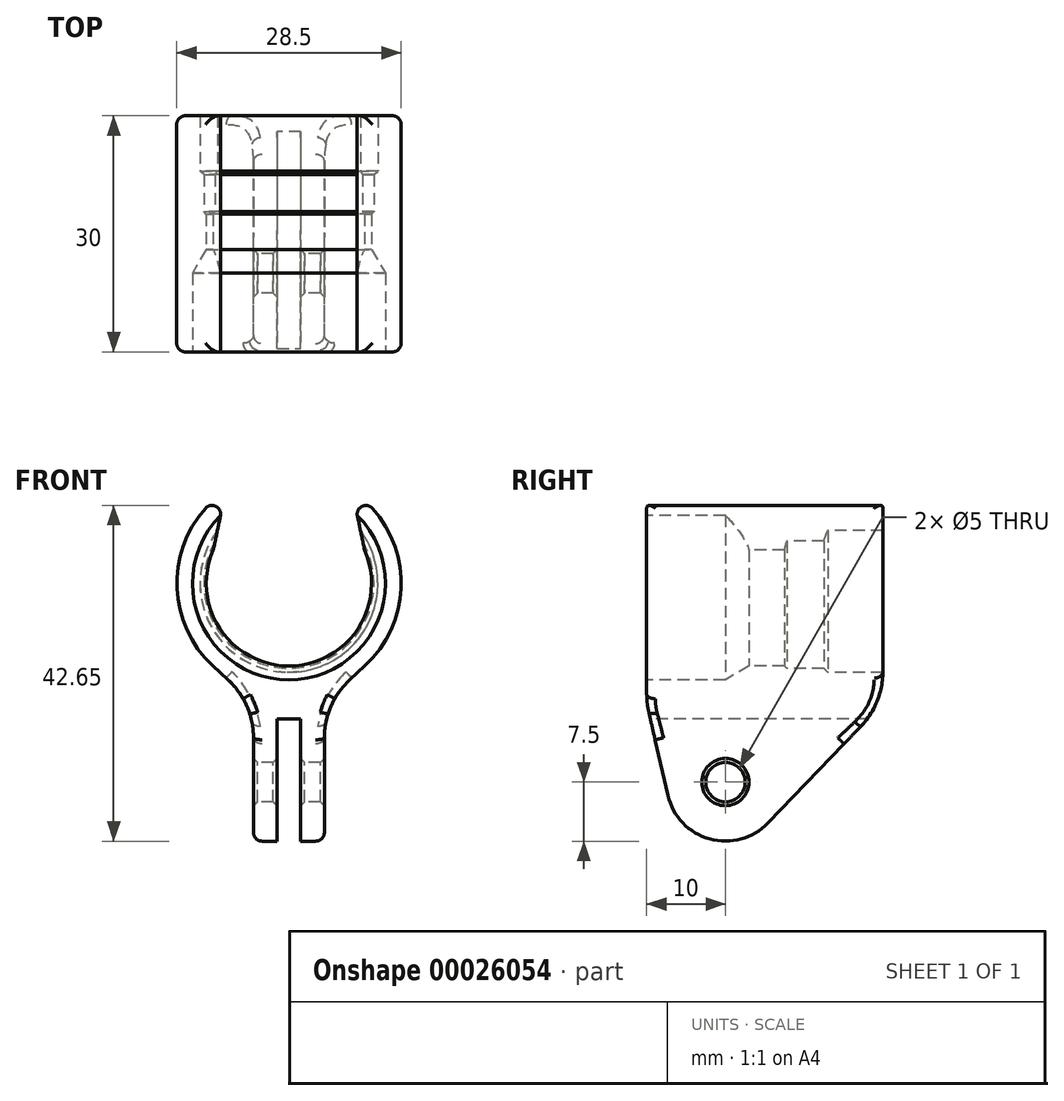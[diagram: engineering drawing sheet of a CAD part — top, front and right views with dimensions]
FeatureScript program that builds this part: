
annotation { "Feature Type Name" : "Feature", "Feature Type Description" : "" }
export const myFeature = defineFeature(function(context is Context, id is Id, definition is map)
    precondition{}
    {
        {
            var Q0;
            Q0=qCreatedBy(makeId("Right.planeOp"),FACE);
            var sketch = newSketch(context, id + "F0", { "sketchPlane" : qUnion([Q0])});
            skLineSegment(sketch, "E0", {"start": v(-10, 12.25) * mm, "end": v(-10, 14.25) * mm});
            skLineSegment(sketch, "E1", {"start": v(-10, 14.25) * mm, "end": v(20, 14.25) * mm});
            skLineSegment(sketch, "E2", {"start": v(20, 14.25) * mm, "end": v(20, 11.3) * mm});
            skLineSegment(sketch, "E3", {"start": v(20, 11.3) * mm, "end": v(13, 11.3) * mm});
            skLineSegment(sketch, "E4", {"start": v(13, 11.3) * mm, "end": v(13, 10.8) * mm});
            skLineSegment(sketch, "E5", {"start": v(13, 10.8) * mm, "end": v(8, 10.8) * mm});
            skLineSegment(sketch, "E6", {"start": v(8, 10.8) * mm, "end": v(8, 10.5) * mm});
            skLineSegment(sketch, "E7", {"start": v(8, 10.5) * mm, "end": v(3, 10.5) * mm});
            skLineSegment(sketch, "E8", {"start": v(0, 12.25) * mm, "end": v(-10, 12.25) * mm});
            skLineSegment(sketch, "E9", {"start": v(3, 10.5) * mm, "end": v(0, 12.25) * mm});
            skLineSegment(sketch, "E10", {"start": v(-10, 0) * mm, "end": v(20, 0) * mm, "construction": true});
            skSolve(sketch);
        }
        {
            var Q0;
            Q0 = qSketchRegion(id + "F0", true);
            var Q1;
            Q1=sQuery(id+"F0.wireOp",EDGE,"E10");
            var Q2;
            Q2=sQuery(id+"F0.wireOp",EDGE,"E10");
            revolve(context, id + "F1", {"entities" : qUnion([Q0]), "surfaceEntities" : qUnion([Q1]), "axis" : qUnion([Q2]), "revolveType" : RevolveType.FULL});
        }
        {
            var Q0;
            Q0=qCreatedBy(makeId("Front.planeOp"),FACE);
            var sketch = newSketch(context, id + "F2", { "sketchPlane" : qUnion([Q0])});
            skLineSegment(sketch, "E11.bottom", {"start": v(7.5, 14.25) * mm, "end": v(-7.5, 14.25) * mm});
            skLineSegment(sketch, "E11.top", {"start": v(10.5, 0) * mm, "end": v(-10.5, 0) * mm});
            skLineSegment(sketch, "E11.left", {"start": v(7.5, 14.25) * mm, "end": v(10.5, 0) * mm});
            skLineSegment(sketch, "E11.right", {"start": v(-7.5, 14.25) * mm, "end": v(-10.5, 0) * mm});
            skSolve(sketch);
        }
        {
            var Q0;
            Q0 = qSketchRegion(id + "F2", true);
            extrude(context, id + "F3", {"entities" : qUnion([Q0]), "operationType" : NewBodyOperationType.REMOVE, "endBound" : BoundingType.THROUGH_ALL, "oppositeDirection" : true, "depth" : 25 * mm, "hasSecondDirection" : true, "secondDirectionBound" : SecondDirectionBoundingType.THROUGH_ALL, "secondDirectionOppositeDirection" : false, "secondDirectionDepth" : 25 * mm});
        }
        {
            var Q0;
            Q0=qCreatedBy(makeId("Front.planeOp"),FACE);
            var sketch = newSketch(context, id + "F4", { "sketchPlane" : qUnion([Q0])});
            skLineSegment(sketch, "E12", {"start": v(-9.68, -10.46) * mm, "end": v(-4.5, -15.25) * mm});
            skLineSegment(sketch, "E13", {"start": v(-4.5, -15.25) * mm, "end": v(4.5, -15.25) * mm});
            skLineSegment(sketch, "E14", {"start": v(4.5, -15.25) * mm, "end": v(9.68, -10.46) * mm});
            skLineSegment(sketch, "E15", {"start": v(0, -15.25) * mm, "end": v(0, 0) * mm, "construction": true});
            skArc(sketch, "E16.0", {"start": v(-9.68, -10.46) * mm, "mid": v(0, -14.25) * mm, "end": v(9.68, -10.46) * mm});
            skPoint(sketch, "E17.orphan", {"position": v(-8.02, 11.78) * mm});
            skPoint(sketch, "E18.orphan", {"position": v(8.02, 11.78) * mm});
            skSolve(sketch);
        }
        {
            var Q0;
            Q0=makeQuery(id+"F4.imprint","IMPRINT",FACE,{"disambiguationData":[TD([[makeQuery(id+"F4.imprint","IMPRINT",EDGE,{"derivedFrom":sQuery(id+"F4.wireOp",EDGE,"E12")}),1.0]])]});
            var Q1;
            Q1=makeQuery(id+"F1.opRevolve","SWEPT_FACE",FACE,{"disambiguationData":[OSD([sQuery(id+"F0.wireOp",EDGE,"E0")])]});
            var Q2;
            Q2=makeQuery(id+"F1.opRevolve","SWEPT_FACE",FACE,{"disambiguationData":[OSD([sQuery(id+"F0.wireOp",EDGE,"E2")])]});
            extrude(context, id + "F5", {"entities" : qUnion([Q0]), "operationType" : NewBodyOperationType.ADD, "endBound" : BoundingType.UP_TO_SURFACE, "endBoundEntityFace" : qUnion([Q1]), "depth" : 2 * mm, "hasSecondDirection" : true, "secondDirectionBound" : SecondDirectionBoundingType.UP_TO_SURFACE, "secondDirectionOppositeDirection" : true, "secondDirectionBoundEntityFace" : qUnion([Q2]), "secondDirectionDepth" : 25 * mm});
        }
        {
            var Q0;
            Q0=qCreatedBy(makeId("Right.planeOp"),FACE);
            var sketch = newSketch(context, id + "F6", { "sketchPlane" : qUnion([Q0])});
            skArc(sketch, "E19", {"start": v(-7.3, -26.93) * mm, "mid": v(-2, -32.48) * mm, "end": v(5.4, -30.44) * mm});
            skCircle(sketch, "E20", {"center": v(0, -25.25) * mm, "radius": 2.5 * mm});
            skLineSegment(sketch, "E21", {"start": v(20, -15.25) * mm, "end": v(5.4, -30.44) * mm});
            skLineSegment(sketch, "E22", {"start": v(-10, -15.25) * mm, "end": v(-7.3, -26.93) * mm});
            skLineSegment(sketch, "E23.0", {"start": v(-10, -15.25) * mm, "end": v(20, -15.25) * mm});
            skSolve(sketch);
        }
        {
            var Q0;
            Q0 = qSketchRegion(id + "F6", true);
            var Q1;
            Q1=makeQuery(id+"F5.opExtrude","SWEPT_FACE",FACE,{"disambiguationData":[OSD([sQuery(id+"F4.wireOp",EDGE,"E12")])]});
            extrude(context, id + "F7", {"entities" : qUnion([Q0]), "operationType" : NewBodyOperationType.ADD, "endBoundEntityFace" : qUnion([Q1]), "depth" : 4.5 * mm, "hasSecondDirection" : true, "secondDirectionOppositeDirection" : true, "secondDirectionDepth" : 4.5 * mm});
        }
        {
            var Q0;
            Q0=qCreatedBy(makeId("Front.planeOp"),FACE);
            var sketch = newSketch(context, id + "F8", { "sketchPlane" : qUnion([Q0])});
            skLineSegment(sketch, "E24.top", {"start": v(1.5, -17.25) * mm, "end": v(-1.5, -17.25) * mm});
            skLineSegment(sketch, "E24.left", {"start": v(1.5, -32.75) * mm, "end": v(1.5, -17.25) * mm});
            skLineSegment(sketch, "E24.right", {"start": v(-1.5, -32.75) * mm, "end": v(-1.5, -17.25) * mm});
            skLineSegment(sketch, "E25", {"start": v(0, 0) * mm, "end": v(0, -32.75) * mm, "construction": true});
            skLineSegment(sketch, "E26", {"start": v(1.5, -32.75) * mm, "end": v(-1.5, -32.75) * mm});
            skSolve(sketch);
        }
        {
            var Q0;
            Q0 = qSketchRegion(id + "F8", true);
            extrude(context, id + "F9", {"entities" : qUnion([Q0]), "operationType" : NewBodyOperationType.REMOVE, "endBound" : BoundingType.THROUGH_ALL, "oppositeDirection" : true, "depth" : 25 * mm, "hasSecondDirection" : true, "secondDirectionBound" : SecondDirectionBoundingType.THROUGH_ALL, "secondDirectionOppositeDirection" : false, "secondDirectionDepth" : 25 * mm});
        }
        {
            var Q0;
            Q0=makeQuery(id+"F7.boolean.opBoolean","MERGE",EDGE,{"derivedFrom":[makeQuery(id+"F5.opExtrude","TWEAK_EDGE",EDGE,{"derivedFrom":[makeQuery(id+"F4.imprint","IMPRINT",EDGE,{"derivedFrom":sQuery(id+"F4.wireOp",EDGE,"E13")}),makeQuery(id+"F4.imprint","IMPRINT",EDGE,{"derivedFrom":sQuery(id+"F4.wireOp",EDGE,"E14")})]}),makeQuery(id+"F7.opExtrude","CAP_EDGE",EDGE,{"disambiguationData":[OSD([sQuery(id+"F6.wireOp",EDGE,"E23.0")])],"isStart":false})]});
            var Q1;
            Q1=makeQuery(id+"F5.opExtrude","TWEAK_EDGE",EDGE,{"derivedFrom":[makeQuery(id+"F4.imprint","IMPRINT",EDGE,{"derivedFrom":sQuery(id+"F4.wireOp",EDGE,"E14")}),makeQuery(id+"F4.imprint","IMPRINT",EDGE,{"derivedFrom":sQuery(id+"F4.wireOp",EDGE,"E16.0")})]});
            var Q2;
            Q2=makeQuery(id+"F7.boolean.opBoolean","MERGE",EDGE,{"derivedFrom":[makeQuery(id+"F5.opExtrude","TWEAK_EDGE",EDGE,{"derivedFrom":[makeQuery(id+"F4.imprint","IMPRINT",EDGE,{"derivedFrom":sQuery(id+"F4.wireOp",EDGE,"E12")}),makeQuery(id+"F4.imprint","IMPRINT",EDGE,{"derivedFrom":sQuery(id+"F4.wireOp",EDGE,"E13")})]}),makeQuery(id+"F7.opExtrude","CAP_EDGE",EDGE,{"disambiguationData":[OSD([sQuery(id+"F6.wireOp",EDGE,"E23.0")])],"isStart":true})]});
            var Q3;
            Q3=makeQuery(id+"F5.opExtrude","TWEAK_EDGE",EDGE,{"derivedFrom":[makeQuery(id+"F4.imprint","IMPRINT",EDGE,{"derivedFrom":sQuery(id+"F4.wireOp",EDGE,"E12")}),makeQuery(id+"F4.imprint","IMPRINT",EDGE,{"derivedFrom":sQuery(id+"F4.wireOp",EDGE,"E16.0")})]});
            var Q4;
            Q4=makeQuery(id+"F7.boolean.opBoolean","MERGE",EDGE,{"derivedFrom":[makeQuery(id+"F5.opExtrude","CAP_EDGE",EDGE,{"disambiguationData":[OSD([sQuery(id+"F4.wireOp",EDGE,"E13")])],"isStart":true}),makeQuery(id+"F7.opExtrude","SWEPT_EDGE",EDGE,{"disambiguationData":[OSD([sQuery(id+"F6.wireOp",EDGE,"E21"),sQuery(id+"F6.wireOp",EDGE,"E23.0")])]})]});
            var Q5;
            Q5=makeQuery(id+"F7.boolean.opBoolean","MERGE",EDGE,{"derivedFrom":[makeQuery(id+"F5.opExtrude","CAP_EDGE",EDGE,{"disambiguationData":[OSD([sQuery(id+"F4.wireOp",EDGE,"E13")])],"isStart":false}),makeQuery(id+"F7.opExtrude","SWEPT_EDGE",EDGE,{"disambiguationData":[OSD([sQuery(id+"F6.wireOp",EDGE,"E22"),sQuery(id+"F6.wireOp",EDGE,"E23.0")])]})]});
            fillet(context, id + "F10", {"entities" : qUnion([Q0, Q1, Q2, Q3, Q4, Q5]), "radius" : 10 * mm, "tangentPropagation" : true, "allowEdgeOverflow" : false});
        }
        {
            var Q0;
            {var subQ0=sQuery(id+"F0.wireOp",EDGE,"E0");var subQ1=sQuery(id+"F0.wireOp",EDGE,"E1");Q0=makeQuery(id+"F5.boolean.opBoolean","SPLIT",EDGE,{"disambiguationData":[TD([makeQuery(id+"F3.boolean.opBoolean","COPY",FACE,{"derivedFrom":makeQuery(id+"F3.opExtrude","SWEPT_FACE",FACE,{"disambiguationData":[OSD([sQuery(id+"F2.wireOp",EDGE,"E11.right")])]})})])],"derivedFrom":makeQuery(id+"F1.opRevolve","SWEPT_EDGE",EDGE,{"disambiguationData":[OSD([subQ0,subQ1])]})});}
            var Q1;
            Q1=makeQuery(id+"F5.opExtrude","CAP_EDGE",EDGE,{"disambiguationData":[OSD([sQuery(id+"F4.wireOp",EDGE,"E12")])],"isStart":false});
            var Q2;
            {var subQ0=sQuery(id+"F4.wireOp",EDGE,"E12");var subQ1=sQuery(id+"F4.wireOp",EDGE,"E13");Q2=makeQuery(id+"F10.opFillet","BLEND_EDGE",EDGE,{"blendedFrom":[makeQuery(id+"F7.boolean.opBoolean","MERGE",EDGE,{"derivedFrom":[makeQuery(id+"F5.opExtrude","TWEAK_EDGE",EDGE,{"derivedFrom":[makeQuery(id+"F4.imprint","IMPRINT",EDGE,{"derivedFrom":subQ0}),makeQuery(id+"F4.imprint","IMPRINT",EDGE,{"derivedFrom":subQ1})]}),makeQuery(id+"F7.opExtrude","CAP_EDGE",EDGE,{"disambiguationData":[OSD([sQuery(id+"F6.wireOp",EDGE,"E23.0")])],"isStart":true})]}),makeQuery(id+"F5.boolean.opBoolean","MERGE",FACE,{"derivedFrom":[makeQuery(id+"F1.opRevolve","SWEPT_FACE",FACE,{"disambiguationData":[OSD([sQuery(id+"F0.wireOp",EDGE,"E0")])]}),makeQuery(id+"F5.opExtrude","CAP_FACE",FACE,{"disambiguationData":[OSD([subQ0,subQ1,sQuery(id+"F4.wireOp",EDGE,"E14"),sQuery(id+"F4.wireOp",EDGE,"E16.0")])],"isStart":false})]})],"blendedInto":[makeQuery(id+"F5.boolean.opBoolean","MERGE",FACE,{"derivedFrom":[makeQuery(id+"F1.opRevolve","SWEPT_FACE",FACE,{"disambiguationData":[OSD([sQuery(id+"F0.wireOp",EDGE,"E0")])]}),makeQuery(id+"F5.opExtrude","CAP_FACE",FACE,{"disambiguationData":[OSD([subQ0,subQ1,sQuery(id+"F4.wireOp",EDGE,"E14"),sQuery(id+"F4.wireOp",EDGE,"E16.0")])],"isStart":false})]})]});}
            var Q3;
            Q3=makeQuery(id+"F10.opFillet","BLEND_EDGE",EDGE,{"blendedFrom":[makeQuery(id+"F7.boolean.opBoolean","MERGE",EDGE,{"derivedFrom":[makeQuery(id+"F5.opExtrude","TWEAK_EDGE",EDGE,{"derivedFrom":[makeQuery(id+"F4.imprint","IMPRINT",EDGE,{"derivedFrom":sQuery(id+"F4.wireOp",EDGE,"E12")}),makeQuery(id+"F4.imprint","IMPRINT",EDGE,{"derivedFrom":sQuery(id+"F4.wireOp",EDGE,"E13")})]}),makeQuery(id+"F7.opExtrude","CAP_EDGE",EDGE,{"disambiguationData":[OSD([sQuery(id+"F6.wireOp",EDGE,"E23.0")])],"isStart":true})]}),makeQuery(id+"F7.opExtrude","SWEPT_FACE",FACE,{"disambiguationData":[OSD([sQuery(id+"F6.wireOp",EDGE,"E22")])]})],"blendedInto":[makeQuery(id+"F7.opExtrude","SWEPT_FACE",FACE,{"disambiguationData":[OSD([sQuery(id+"F6.wireOp",EDGE,"E22")])]})]});
            var Q4;
            Q4=makeQuery(id+"F7.opExtrude","CAP_EDGE",EDGE,{"disambiguationData":[OSD([sQuery(id+"F6.wireOp",EDGE,"E22")])],"isStart":true});
            var Q5;
            Q5=makeQuery(id+"F7.opExtrude","CAP_EDGE",EDGE,{"disambiguationData":[OSD([sQuery(id+"F6.wireOp",EDGE,"E19")])],"isStart":true});
            var Q6;
            Q6=makeQuery(id+"F7.opExtrude","CAP_EDGE",EDGE,{"disambiguationData":[OSD([sQuery(id+"F6.wireOp",EDGE,"E21")])],"isStart":true});
            var Q7;
            Q7=makeQuery(id+"F10.opFillet","BLEND_EDGE",EDGE,{"blendedFrom":[makeQuery(id+"F7.boolean.opBoolean","MERGE",EDGE,{"derivedFrom":[makeQuery(id+"F5.opExtrude","TWEAK_EDGE",EDGE,{"derivedFrom":[makeQuery(id+"F4.imprint","IMPRINT",EDGE,{"derivedFrom":sQuery(id+"F4.wireOp",EDGE,"E12")}),makeQuery(id+"F4.imprint","IMPRINT",EDGE,{"derivedFrom":sQuery(id+"F4.wireOp",EDGE,"E13")})]}),makeQuery(id+"F7.opExtrude","CAP_EDGE",EDGE,{"disambiguationData":[OSD([sQuery(id+"F6.wireOp",EDGE,"E23.0")])],"isStart":true})]}),makeQuery(id+"F7.opExtrude","SWEPT_FACE",FACE,{"disambiguationData":[OSD([sQuery(id+"F6.wireOp",EDGE,"E21")])]})],"blendedInto":[makeQuery(id+"F7.opExtrude","SWEPT_FACE",FACE,{"disambiguationData":[OSD([sQuery(id+"F6.wireOp",EDGE,"E21")])]})]});
            var Q8;
            {var subQ0=sQuery(id+"F4.wireOp",EDGE,"E12");var subQ1=sQuery(id+"F4.wireOp",EDGE,"E13");Q8=makeQuery(id+"F10.opFillet","BLEND_EDGE",EDGE,{"blendedFrom":[makeQuery(id+"F7.boolean.opBoolean","MERGE",EDGE,{"derivedFrom":[makeQuery(id+"F5.opExtrude","TWEAK_EDGE",EDGE,{"derivedFrom":[makeQuery(id+"F4.imprint","IMPRINT",EDGE,{"derivedFrom":subQ0}),makeQuery(id+"F4.imprint","IMPRINT",EDGE,{"derivedFrom":subQ1})]}),makeQuery(id+"F7.opExtrude","CAP_EDGE",EDGE,{"disambiguationData":[OSD([sQuery(id+"F6.wireOp",EDGE,"E23.0")])],"isStart":true})]}),makeQuery(id+"F5.boolean.opBoolean","MERGE",FACE,{"derivedFrom":[makeQuery(id+"F1.opRevolve","SWEPT_FACE",FACE,{"disambiguationData":[OSD([sQuery(id+"F0.wireOp",EDGE,"E2")])]}),makeQuery(id+"F5.opExtrude","CAP_FACE",FACE,{"disambiguationData":[OSD([subQ0,subQ1,sQuery(id+"F4.wireOp",EDGE,"E14"),sQuery(id+"F4.wireOp",EDGE,"E16.0")])],"isStart":true})]})],"blendedInto":[makeQuery(id+"F5.boolean.opBoolean","MERGE",FACE,{"derivedFrom":[makeQuery(id+"F1.opRevolve","SWEPT_FACE",FACE,{"disambiguationData":[OSD([sQuery(id+"F0.wireOp",EDGE,"E2")])]}),makeQuery(id+"F5.opExtrude","CAP_FACE",FACE,{"disambiguationData":[OSD([subQ0,subQ1,sQuery(id+"F4.wireOp",EDGE,"E14"),sQuery(id+"F4.wireOp",EDGE,"E16.0")])],"isStart":true})]})]});}
            var Q9;
            Q9=makeQuery(id+"F5.opExtrude","CAP_EDGE",EDGE,{"disambiguationData":[OSD([sQuery(id+"F4.wireOp",EDGE,"E12")])],"isStart":true});
            var Q10;
            {var subQ0=sQuery(id+"F0.wireOp",EDGE,"E1");var subQ1=sQuery(id+"F0.wireOp",EDGE,"E2");Q10=makeQuery(id+"F5.boolean.opBoolean","SPLIT",EDGE,{"disambiguationData":[TD([makeQuery(id+"F3.boolean.opBoolean","COPY",FACE,{"derivedFrom":makeQuery(id+"F3.opExtrude","SWEPT_FACE",FACE,{"disambiguationData":[OSD([sQuery(id+"F2.wireOp",EDGE,"E11.right")])]})})])],"derivedFrom":makeQuery(id+"F1.opRevolve","SWEPT_EDGE",EDGE,{"disambiguationData":[OSD([subQ0,subQ1])]})});}
            var Q11;
            Q11=makeQuery(id+"F3.boolean.opBoolean","INTERSECT",EDGE,{"derivedFrom":[makeQuery(id+"F1.opRevolve","SWEPT_FACE",FACE,{"disambiguationData":[OSD([sQuery(id+"F0.wireOp",EDGE,"E1")])]}),makeQuery(id+"F3.opExtrude","SWEPT_FACE",FACE,{"disambiguationData":[OSD([sQuery(id+"F2.wireOp",EDGE,"E11.right")])]})]});
            var Q12;
            Q12=makeQuery(id+"F3.boolean.opBoolean","INTERSECT",EDGE,{"derivedFrom":[makeQuery(id+"F1.opRevolve","SWEPT_FACE",FACE,{"disambiguationData":[OSD([sQuery(id+"F0.wireOp",EDGE,"E1")])]}),makeQuery(id+"F3.opExtrude","SWEPT_FACE",FACE,{"disambiguationData":[OSD([sQuery(id+"F2.wireOp",EDGE,"E11.left")])]})]});
            var Q13;
            {var subQ0=sQuery(id+"F0.wireOp",EDGE,"E0");var subQ1=sQuery(id+"F0.wireOp",EDGE,"E1");Q13=makeQuery(id+"F5.boolean.opBoolean","SPLIT",EDGE,{"disambiguationData":[TD([makeQuery(id+"F3.boolean.opBoolean","COPY",FACE,{"derivedFrom":makeQuery(id+"F3.opExtrude","SWEPT_FACE",FACE,{"disambiguationData":[OSD([sQuery(id+"F2.wireOp",EDGE,"E11.left")])]})})])],"derivedFrom":makeQuery(id+"F1.opRevolve","SWEPT_EDGE",EDGE,{"disambiguationData":[OSD([subQ0,subQ1])]})});}
            var Q14;
            Q14=makeQuery(id+"F5.opExtrude","CAP_EDGE",EDGE,{"disambiguationData":[OSD([sQuery(id+"F4.wireOp",EDGE,"E14")])],"isStart":false});
            var Q15;
            {var subQ0=sQuery(id+"F4.wireOp",EDGE,"E13");var subQ1=sQuery(id+"F4.wireOp",EDGE,"E14");Q15=makeQuery(id+"F10.opFillet","BLEND_EDGE",EDGE,{"blendedFrom":[makeQuery(id+"F7.boolean.opBoolean","MERGE",EDGE,{"derivedFrom":[makeQuery(id+"F5.opExtrude","TWEAK_EDGE",EDGE,{"derivedFrom":[makeQuery(id+"F4.imprint","IMPRINT",EDGE,{"derivedFrom":subQ0}),makeQuery(id+"F4.imprint","IMPRINT",EDGE,{"derivedFrom":subQ1})]}),makeQuery(id+"F7.opExtrude","CAP_EDGE",EDGE,{"disambiguationData":[OSD([sQuery(id+"F6.wireOp",EDGE,"E23.0")])],"isStart":false})]}),makeQuery(id+"F5.boolean.opBoolean","MERGE",FACE,{"derivedFrom":[makeQuery(id+"F1.opRevolve","SWEPT_FACE",FACE,{"disambiguationData":[OSD([sQuery(id+"F0.wireOp",EDGE,"E0")])]}),makeQuery(id+"F5.opExtrude","CAP_FACE",FACE,{"disambiguationData":[OSD([sQuery(id+"F4.wireOp",EDGE,"E12"),subQ0,subQ1,sQuery(id+"F4.wireOp",EDGE,"E16.0")])],"isStart":false})]})],"blendedInto":[makeQuery(id+"F5.boolean.opBoolean","MERGE",FACE,{"derivedFrom":[makeQuery(id+"F1.opRevolve","SWEPT_FACE",FACE,{"disambiguationData":[OSD([sQuery(id+"F0.wireOp",EDGE,"E0")])]}),makeQuery(id+"F5.opExtrude","CAP_FACE",FACE,{"disambiguationData":[OSD([sQuery(id+"F4.wireOp",EDGE,"E12"),subQ0,subQ1,sQuery(id+"F4.wireOp",EDGE,"E16.0")])],"isStart":false})]})]});}
            var Q16;
            Q16=makeQuery(id+"F10.opFillet","BLEND_EDGE",EDGE,{"blendedFrom":[makeQuery(id+"F7.boolean.opBoolean","MERGE",EDGE,{"derivedFrom":[makeQuery(id+"F5.opExtrude","TWEAK_EDGE",EDGE,{"derivedFrom":[makeQuery(id+"F4.imprint","IMPRINT",EDGE,{"derivedFrom":sQuery(id+"F4.wireOp",EDGE,"E13")}),makeQuery(id+"F4.imprint","IMPRINT",EDGE,{"derivedFrom":sQuery(id+"F4.wireOp",EDGE,"E14")})]}),makeQuery(id+"F7.opExtrude","CAP_EDGE",EDGE,{"disambiguationData":[OSD([sQuery(id+"F6.wireOp",EDGE,"E23.0")])],"isStart":false})]}),makeQuery(id+"F7.opExtrude","SWEPT_FACE",FACE,{"disambiguationData":[OSD([sQuery(id+"F6.wireOp",EDGE,"E22")])]})],"blendedInto":[makeQuery(id+"F7.opExtrude","SWEPT_FACE",FACE,{"disambiguationData":[OSD([sQuery(id+"F6.wireOp",EDGE,"E22")])]})]});
            var Q17;
            Q17=makeQuery(id+"F7.opExtrude","CAP_EDGE",EDGE,{"disambiguationData":[OSD([sQuery(id+"F6.wireOp",EDGE,"E22")])],"isStart":false});
            var Q18;
            Q18=makeQuery(id+"F7.opExtrude","CAP_EDGE",EDGE,{"disambiguationData":[OSD([sQuery(id+"F6.wireOp",EDGE,"E19")])],"isStart":false});
            var Q19;
            Q19=makeQuery(id+"F7.opExtrude","CAP_EDGE",EDGE,{"disambiguationData":[OSD([sQuery(id+"F6.wireOp",EDGE,"E21")])],"isStart":false});
            var Q20;
            Q20=makeQuery(id+"F10.opFillet","BLEND_EDGE",EDGE,{"blendedFrom":[makeQuery(id+"F7.boolean.opBoolean","MERGE",EDGE,{"derivedFrom":[makeQuery(id+"F5.opExtrude","TWEAK_EDGE",EDGE,{"derivedFrom":[makeQuery(id+"F4.imprint","IMPRINT",EDGE,{"derivedFrom":sQuery(id+"F4.wireOp",EDGE,"E13")}),makeQuery(id+"F4.imprint","IMPRINT",EDGE,{"derivedFrom":sQuery(id+"F4.wireOp",EDGE,"E14")})]}),makeQuery(id+"F7.opExtrude","CAP_EDGE",EDGE,{"disambiguationData":[OSD([sQuery(id+"F6.wireOp",EDGE,"E23.0")])],"isStart":false})]}),makeQuery(id+"F7.opExtrude","SWEPT_FACE",FACE,{"disambiguationData":[OSD([sQuery(id+"F6.wireOp",EDGE,"E21")])]})],"blendedInto":[makeQuery(id+"F7.opExtrude","SWEPT_FACE",FACE,{"disambiguationData":[OSD([sQuery(id+"F6.wireOp",EDGE,"E21")])]})]});
            var Q21;
            {var subQ0=sQuery(id+"F4.wireOp",EDGE,"E13");var subQ1=sQuery(id+"F4.wireOp",EDGE,"E14");Q21=makeQuery(id+"F10.opFillet","BLEND_EDGE",EDGE,{"blendedFrom":[makeQuery(id+"F7.boolean.opBoolean","MERGE",EDGE,{"derivedFrom":[makeQuery(id+"F5.opExtrude","TWEAK_EDGE",EDGE,{"derivedFrom":[makeQuery(id+"F4.imprint","IMPRINT",EDGE,{"derivedFrom":subQ0}),makeQuery(id+"F4.imprint","IMPRINT",EDGE,{"derivedFrom":subQ1})]}),makeQuery(id+"F7.opExtrude","CAP_EDGE",EDGE,{"disambiguationData":[OSD([sQuery(id+"F6.wireOp",EDGE,"E23.0")])],"isStart":false})]}),makeQuery(id+"F5.boolean.opBoolean","MERGE",FACE,{"derivedFrom":[makeQuery(id+"F1.opRevolve","SWEPT_FACE",FACE,{"disambiguationData":[OSD([sQuery(id+"F0.wireOp",EDGE,"E2")])]}),makeQuery(id+"F5.opExtrude","CAP_FACE",FACE,{"disambiguationData":[OSD([sQuery(id+"F4.wireOp",EDGE,"E12"),subQ0,subQ1,sQuery(id+"F4.wireOp",EDGE,"E16.0")])],"isStart":true})]})],"blendedInto":[makeQuery(id+"F5.boolean.opBoolean","MERGE",FACE,{"derivedFrom":[makeQuery(id+"F1.opRevolve","SWEPT_FACE",FACE,{"disambiguationData":[OSD([sQuery(id+"F0.wireOp",EDGE,"E2")])]}),makeQuery(id+"F5.opExtrude","CAP_FACE",FACE,{"disambiguationData":[OSD([sQuery(id+"F4.wireOp",EDGE,"E12"),subQ0,subQ1,sQuery(id+"F4.wireOp",EDGE,"E16.0")])],"isStart":true})]})]});}
            var Q22;
            Q22=makeQuery(id+"F5.opExtrude","CAP_EDGE",EDGE,{"disambiguationData":[OSD([sQuery(id+"F4.wireOp",EDGE,"E14")])],"isStart":true});
            var Q23;
            {var subQ0=sQuery(id+"F0.wireOp",EDGE,"E1");var subQ1=sQuery(id+"F0.wireOp",EDGE,"E2");Q23=makeQuery(id+"F5.boolean.opBoolean","SPLIT",EDGE,{"disambiguationData":[TD([makeQuery(id+"F3.boolean.opBoolean","COPY",FACE,{"derivedFrom":makeQuery(id+"F3.opExtrude","SWEPT_FACE",FACE,{"disambiguationData":[OSD([sQuery(id+"F2.wireOp",EDGE,"E11.left")])]})})])],"derivedFrom":makeQuery(id+"F1.opRevolve","SWEPT_EDGE",EDGE,{"disambiguationData":[OSD([subQ0,subQ1])]})});}
            fillet(context, id + "F11", {"entities" : qUnion([Q0, Q1, Q2, Q3, Q4, Q5, Q6, Q7, Q8, Q9, Q10, Q11, Q12, Q13, Q14, Q15, Q16, Q17, Q18, Q19, Q20, Q21, Q22, Q23]), "radius" : 1.1 * mm, "tangentPropagation" : true, "allowEdgeOverflow" : false});
        }
        {
            var Q0;
            Q0=makeQuery(id+"F1.opRevolve","SWEPT_EDGE",EDGE,{"disambiguationData":[OSD([sQuery(id+"F0.wireOp",EDGE,"E4"),sQuery(id+"F0.wireOp",EDGE,"E5")])]});
            var Q1;
            Q1=makeQuery(id+"F1.opRevolve","SWEPT_EDGE",EDGE,{"disambiguationData":[OSD([sQuery(id+"F0.wireOp",EDGE,"E6"),sQuery(id+"F0.wireOp",EDGE,"E7")])]});
            var Q2;
            Q2=makeQuery(id+"F7.opExtrude","CAP_EDGE",EDGE,{"disambiguationData":[OSD([sQuery(id+"F6.wireOp",EDGE,"E20")])],"isStart":false});
            var Q3;
            Q3=makeQuery(id+"F9.boolean.opBoolean","INTERSECT",EDGE,{"derivedFrom":[makeQuery(id+"F7.opExtrude","SWEPT_FACE",FACE,{"disambiguationData":[OSD([sQuery(id+"F6.wireOp",EDGE,"E20")])]}),makeQuery(id+"F9.opExtrude","SWEPT_FACE",FACE,{"disambiguationData":[OSD([sQuery(id+"F8.wireOp",EDGE,"E24.left")])]})]});
            var Q4;
            Q4=makeQuery(id+"F9.boolean.opBoolean","INTERSECT",EDGE,{"derivedFrom":[makeQuery(id+"F7.opExtrude","SWEPT_FACE",FACE,{"disambiguationData":[OSD([sQuery(id+"F6.wireOp",EDGE,"E20")])]}),makeQuery(id+"F9.opExtrude","SWEPT_FACE",FACE,{"disambiguationData":[OSD([sQuery(id+"F8.wireOp",EDGE,"E24.right")])]})]});
            var Q5;
            Q5=makeQuery(id+"F7.opExtrude","CAP_EDGE",EDGE,{"disambiguationData":[OSD([sQuery(id+"F6.wireOp",EDGE,"E20")])],"isStart":true});
            chamfer(context, id + "F12", {"entities" : qUnion([Q0, Q1, Q2, Q3, Q4, Q5]), "width" : 0.5 * mm, "tangentPropagation" : true});
        }
    });
